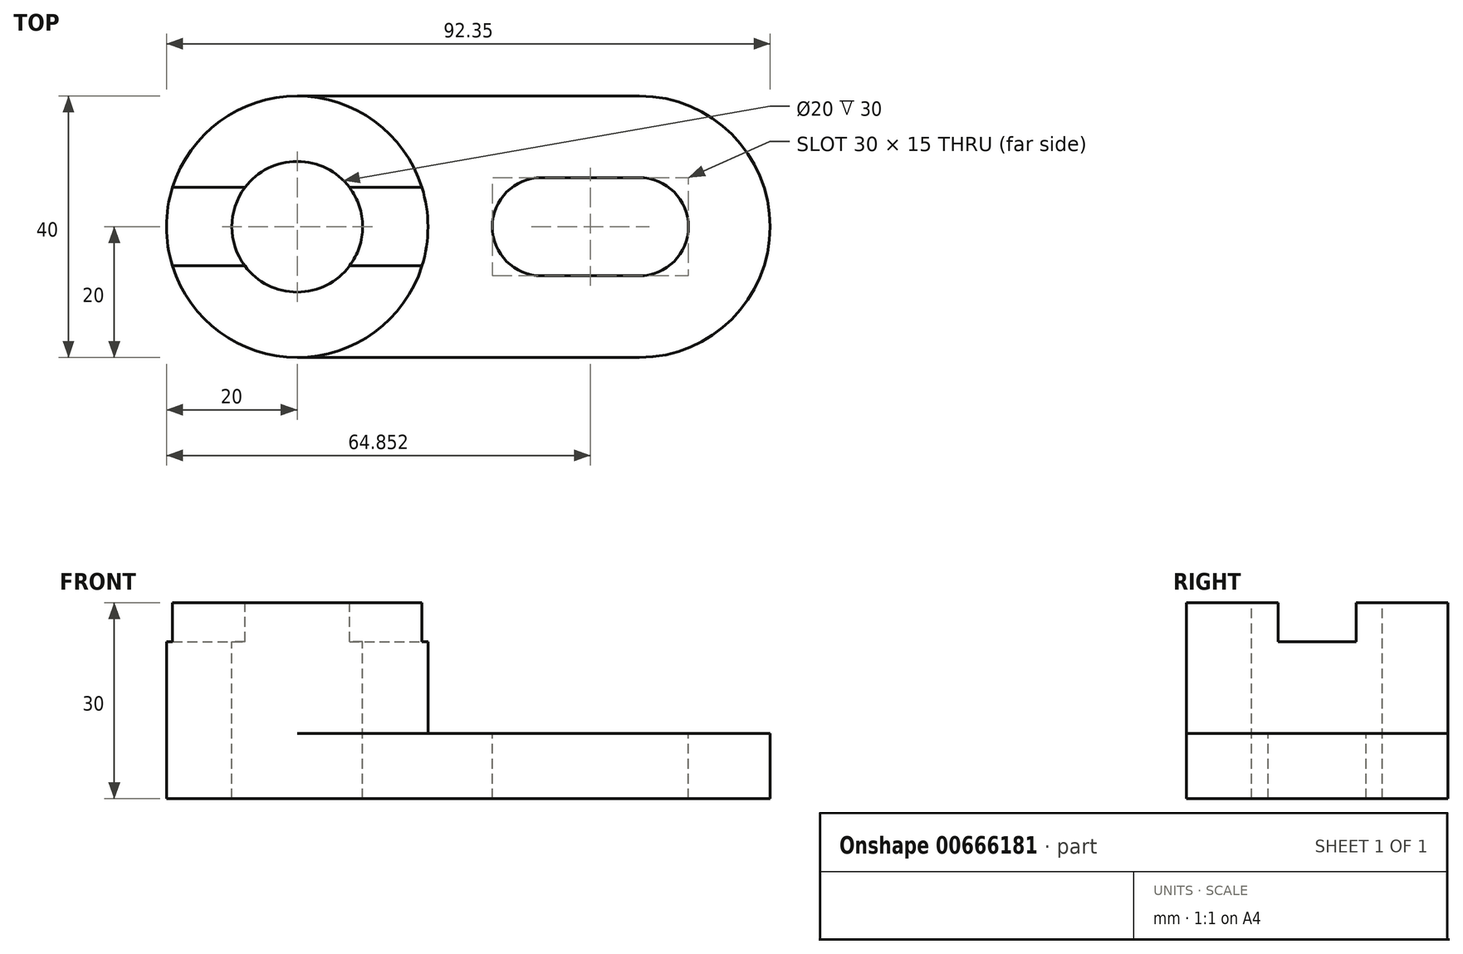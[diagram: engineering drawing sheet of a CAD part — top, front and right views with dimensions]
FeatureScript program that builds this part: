
annotation { "Feature Type Name" : "Feature", "Feature Type Description" : "" }
export const myFeature = defineFeature(function(context is Context, id is Id, definition is map)
    precondition{}
    {
        {
            var Q0;
            Q0=qCreatedBy(makeId("Top.planeOp"),FACE);
            var sketch = newSketch(context, id + "F0", { "sketchPlane" : qUnion([Q0])});
            skArc(sketch, "E0", {"start": v(0, 20) * mm, "mid": v(-20, 0) * mm, "end": v(0, -20) * mm});
            skArc(sketch, "E1", {"start": v(52.35, -20) * mm, "mid": v(72.35, 0) * mm, "end": v(52.35, 20) * mm});
            skLineSegment(sketch, "E2", {"start": v(0, 20) * mm, "end": v(52.35, 20) * mm});
            skLineSegment(sketch, "E3", {"start": v(0, -20) * mm, "end": v(52.35, -20) * mm});
            skSolve(sketch);
        }
        {
            var Q0;
            Q0=makeQuery(id+"F0.imprint","IMPRINT",FACE,{"disambiguationData":[TD([[makeQuery(id+"F0.imprint","IMPRINT",EDGE,{"derivedFrom":sQuery(id+"F0.wireOp",EDGE,"E0")}),1.0]])]});
            extrude(context, id + "F1", {"entities" : qUnion([Q0]), "depth" : 10 * mm, "offsetDistance" : 25 * mm});
        }
        {
            var Q0;
            Q0=makeQuery(id+"F1.opExtrude","CAP_FACE",FACE,{"disambiguationData":[OSD([sQuery(id+"F0.wireOp",EDGE,"E0"),sQuery(id+"F0.wireOp",EDGE,"E1"),sQuery(id+"F0.wireOp",EDGE,"E2"),sQuery(id+"F0.wireOp",EDGE,"E3")])],"isStart":false});
            var sketch = newSketch(context, id + "F2", { "sketchPlane" : qUnion([Q0])});
            skCircle(sketch, "E4", {"center": v(0, 0) * mm, "radius": 20 * mm});
            skSolve(sketch);
        }
        {
            var Q0;
            {var subQ0=sQuery(id+"F2.wireOp",EDGE,"E4");var subQ1=makeQuery(id+"F2.imprint","INTERSECT",VERTEX,{"derivedFrom":[makeQuery(id+"F1.opExtrude","CAP_EDGE",EDGE,{"disambiguationData":[OSD([sQuery(id+"F0.wireOp",EDGE,"E2")])],"isStart":false}),subQ0]});Q0=makeQuery(id+"F2.imprint","IMPRINT",FACE,{"disambiguationData":[TD([[makeQuery(id+"F2.imprint","IMPRINT",EDGE,{"disambiguationData":[TD([[subQ1,-1.0]])],"derivedFrom":subQ0}),1.0]])]});}
            extrude(context, id + "F3", {"entities" : qUnion([Q0]), "operationType" : NewBodyOperationType.ADD, "depth" : 20 * mm, "offsetDistance" : 25 * mm});
        }
        {
            var Q0;
            Q0=makeQuery(id+"F3.opExtrude","CAP_FACE",FACE,{"disambiguationData":[OSD([sQuery(id+"F2.wireOp",EDGE,"E4")])],"isStart":false});
            var sketch = newSketch(context, id + "F4", { "sketchPlane" : qUnion([Q0])});
            skCircle(sketch, "E5", {"center": v(0, 0) * mm, "radius": 10 * mm});
            skSolve(sketch);
        }
        {
            var Q0;
            Q0=makeQuery(id+"F4.imprint","IMPRINT",FACE,{"disambiguationData":[TD([[makeQuery(id+"F4.imprint","IMPRINT",EDGE,{"derivedFrom":sQuery(id+"F4.wireOp",EDGE,"E5")}),1.0]])]});
            extrude(context, id + "F5", {"entities" : qUnion([Q0]), "operationType" : NewBodyOperationType.REMOVE, "oppositeDirection" : true, "depth" : 50 * mm, "offsetDistance" : 25 * mm});
        }
        {
            var Q0;
            Q0=makeQuery(id+"F3.opExtrude","CAP_FACE",FACE,{"disambiguationData":[OSD([sQuery(id+"F2.wireOp",EDGE,"E4")])],"isStart":false});
            var sketch = newSketch(context, id + "F6", { "sketchPlane" : qUnion([Q0])});
            skLineSegment(sketch, "E6.bottom", {"start": v(-25.13, 6) * mm, "end": v(24.87, 6) * mm});
            skLineSegment(sketch, "E6.top", {"start": v(-25.13, -6) * mm, "end": v(24.87, -6) * mm});
            skLineSegment(sketch, "E6.left", {"start": v(-25.13, 6) * mm, "end": v(-25.13, -6) * mm});
            skLineSegment(sketch, "E6.right", {"start": v(24.87, 6) * mm, "end": v(24.87, -6) * mm});
            skSolve(sketch);
        }
        {
            var Q0;
            {var subQ0=sQuery(id+"F6.wireOp",EDGE,"E6.right");Q0=makeQuery(id+"F6.imprint","IMPRINT",FACE,{"disambiguationData":[TD([[makeQuery(id+"F6.imprint","IMPRINT",EDGE,{"derivedFrom":subQ0}),-1.0]])]});}
            var Q1;
            {var subQ0=sQuery(id+"F6.wireOp",EDGE,"E6.bottom");var subQ1=makeQuery(id+"F3.opExtrude","CAP_EDGE",EDGE,{"disambiguationData":[OSD([sQuery(id+"F2.wireOp",EDGE,"E4")])],"isStart":false});var subQ2=makeQuery(id+"F6.imprint","INTERSECT",VERTEX,{"disambiguationData":[OD(0.0)],"derivedFrom":[subQ1,subQ0]});Q1=makeQuery(id+"F6.imprint","IMPRINT",FACE,{"disambiguationData":[TD([[makeQuery(id+"F6.imprint","IMPRINT",EDGE,{"disambiguationData":[TD([[subQ2,-1.0]])],"derivedFrom":subQ0}),-1.0]])]});}
            var Q2;
            {var subQ0=sQuery(id+"F6.wireOp",EDGE,"E6.bottom");var subQ1=makeQuery(id+"F5.boolean.opBoolean","COPY",EDGE,{"derivedFrom":makeQuery(id+"F5.opExtrude","CAP_EDGE",EDGE,{"disambiguationData":[OSD([sQuery(id+"F4.wireOp",EDGE,"E5")])],"isStart":true})});var subQ2=makeQuery(id+"F6.imprint","INTERSECT",VERTEX,{"disambiguationData":[OD(0.0)],"derivedFrom":[subQ1,subQ0]});Q2=makeQuery(id+"F6.imprint","IMPRINT",FACE,{"disambiguationData":[TD([[makeQuery(id+"F6.imprint","IMPRINT",EDGE,{"disambiguationData":[TD([[subQ2,-1.0]])],"derivedFrom":subQ0}),-1.0]])]});}
            var Q3;
            {var subQ0=sQuery(id+"F6.wireOp",EDGE,"E6.bottom");var subQ1=makeQuery(id+"F3.opExtrude","CAP_EDGE",EDGE,{"disambiguationData":[OSD([sQuery(id+"F2.wireOp",EDGE,"E4")])],"isStart":false});var subQ2=makeQuery(id+"F6.imprint","INTERSECT",VERTEX,{"disambiguationData":[OD(1.0)],"derivedFrom":[subQ1,subQ0]});Q3=makeQuery(id+"F6.imprint","IMPRINT",FACE,{"disambiguationData":[TD([[makeQuery(id+"F6.imprint","IMPRINT",EDGE,{"disambiguationData":[TD([[subQ2,1.0]])],"derivedFrom":subQ0}),-1.0]])]});}
            extrude(context, id + "F7", {"entities" : qUnion([Q0, Q1, Q2, Q3]), "operationType" : NewBodyOperationType.REMOVE, "oppositeDirection" : true, "depth" : 6 * mm, "offsetDistance" : 25 * mm});
        }
        {
            var Q0;
            Q0=makeQuery(id+"F1.opExtrude","CAP_FACE",FACE,{"disambiguationData":[OSD([sQuery(id+"F0.wireOp",EDGE,"E0"),sQuery(id+"F0.wireOp",EDGE,"E1"),sQuery(id+"F0.wireOp",EDGE,"E2"),sQuery(id+"F0.wireOp",EDGE,"E3")])],"isStart":false});
            var sketch = newSketch(context, id + "F8", { "sketchPlane" : qUnion([Q0])});
            skArc(sketch, "E7", {"start": v(37.35, 7.5) * mm, "mid": v(29.85, 0) * mm, "end": v(37.35, -7.5) * mm});
            skArc(sketch, "E8", {"start": v(52.35, -7.5) * mm, "mid": v(59.85, 0) * mm, "end": v(52.35, 7.5) * mm});
            skLineSegment(sketch, "E9", {"start": v(52.35, -7.5) * mm, "end": v(37.35, -7.5) * mm});
            skLineSegment(sketch, "E10", {"start": v(37.35, 7.5) * mm, "end": v(52.35, 7.5) * mm});
            skSolve(sketch);
        }
        {
            var Q0;
            Q0=makeQuery(id+"F8.imprint","IMPRINT",FACE,{"disambiguationData":[TD([[makeQuery(id+"F8.imprint","IMPRINT",EDGE,{"derivedFrom":sQuery(id+"F8.wireOp",EDGE,"E7")}),1.0]])]});
            extrude(context, id + "F9", {"entities" : qUnion([Q0]), "operationType" : NewBodyOperationType.REMOVE, "oppositeDirection" : true, "depth" : 25 * mm, "offsetDistance" : 25 * mm});
        }
    });
